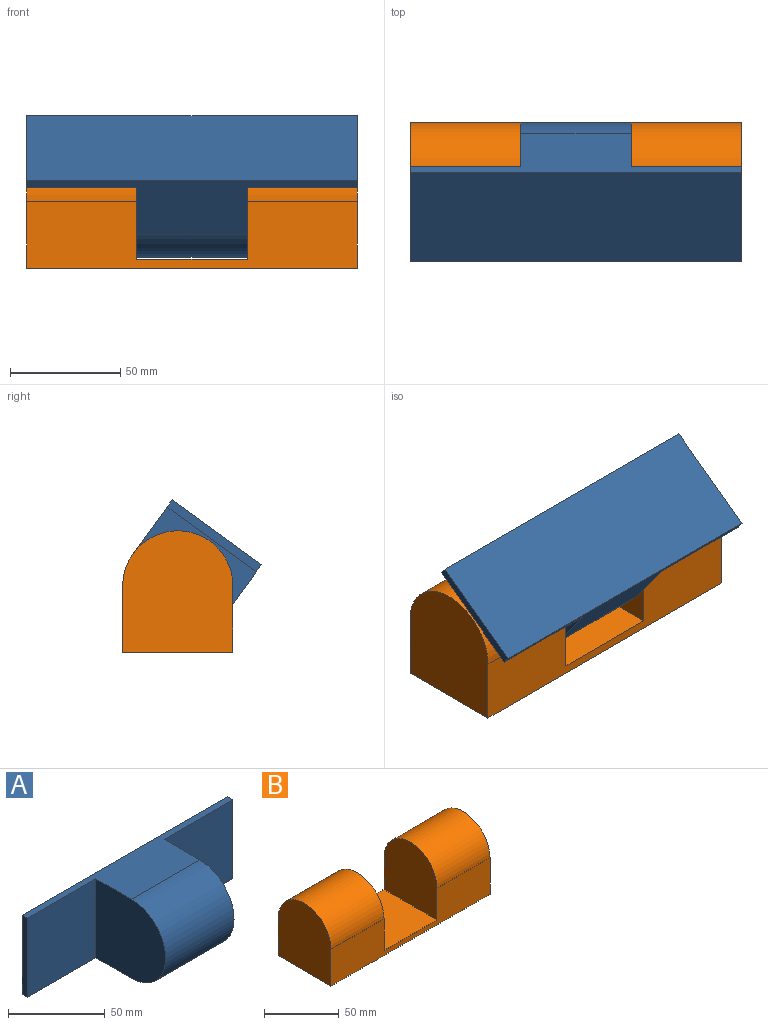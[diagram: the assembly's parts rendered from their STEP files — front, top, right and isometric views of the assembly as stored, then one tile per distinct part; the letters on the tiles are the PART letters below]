
ASSEMBLY  parts=2 mates=1
PART A: 10 faces, bbox 150x55x50 mm
  f0: plane 150x30mm, normal (0,0,1), area 1900mm2, adj f2,f3,f4,f5,f6,f7,f8,f9
  f1: plane 150x30mm, normal (0,0,-1), area 1900mm2, adj f2,f3,f4,f5,f6,f7,f8,f9
  f2: cylinder r=25mm len=50mm, axis (-1,0,0), area 3927mm2, adj f0,f1,f7,f9
  f3: plane 150x50mm, normal (0,1,0), area 7500mm2, adj f0,f1,f4,f5
  f4: plane 50x4mm, normal (1,0,0), area 200mm2, adj f0,f1,f3,f8
  f5: plane 50x4mm, normal (-1,0,0), area 200mm2, adj f0,f1,f3,f6
  f6: plane 50x50mm, normal (0,-1,0), area 2500mm2, adj f0,f1,f5,f7
  f7: plane 51x50mm, normal (-1,0,0), area 2281.7mm2, adj f0,f1,f2,f6
  f8: plane 50x50mm, normal (0,-1,0), area 2500mm2, adj f0,f1,f4,f9
  f9: plane 51x50mm, normal (1,0,0), area 2281.7mm2, adj f0,f1,f2,f8
PART B: 10 faces, bbox 150x50x55 mm
  f0: cylinder r=25mm len=50mm, axis (-1,0,0), area 3927mm2, adj f1,f2,f4,f9
  f1: plane 150x30mm, normal (0,1,0), area 3200mm2, adj f0,f3,f4,f5,f6,f7,f8,f9
  f2: plane 150x30mm, normal (0,-1,0), area 3200mm2, adj f0,f3,f4,f5,f6,f7,f8,f9
  f3: plane 150x50mm, normal (0,0,-1), area 7500mm2, adj f1,f2,f4,f5
  f4: plane 55x50mm, normal (1,0,0), area 2481.7mm2, adj f0,f1,f2,f3
  f5: plane 55x50mm, normal (-1,0,0), area 2481.7mm2, adj f1,f2,f3,f6
  f6: cylinder r=25mm len=50mm, axis (-1,0,0), area 3927mm2, adj f1,f2,f5,f8
  f7: plane 50x50mm, normal (0,0,1), area 2500mm2, adj f1,f2,f8,f9
  f8: plane 51x50mm, normal (1,0,0), area 2281.7mm2, adj f1,f2,f6,f7
  f9: plane 51x50mm, normal (-1,0,0), area 2281.7mm2, adj f0,f1,f2,f7
PLACE A rot(axis=(1,0,0),126.1deg) t=(0,-3.97,2.02)mm
PLACE B at identity
MATE revolute A.f2 <-> B.f0  axis (-1,0,0) through (100,-2.5,0)mm
